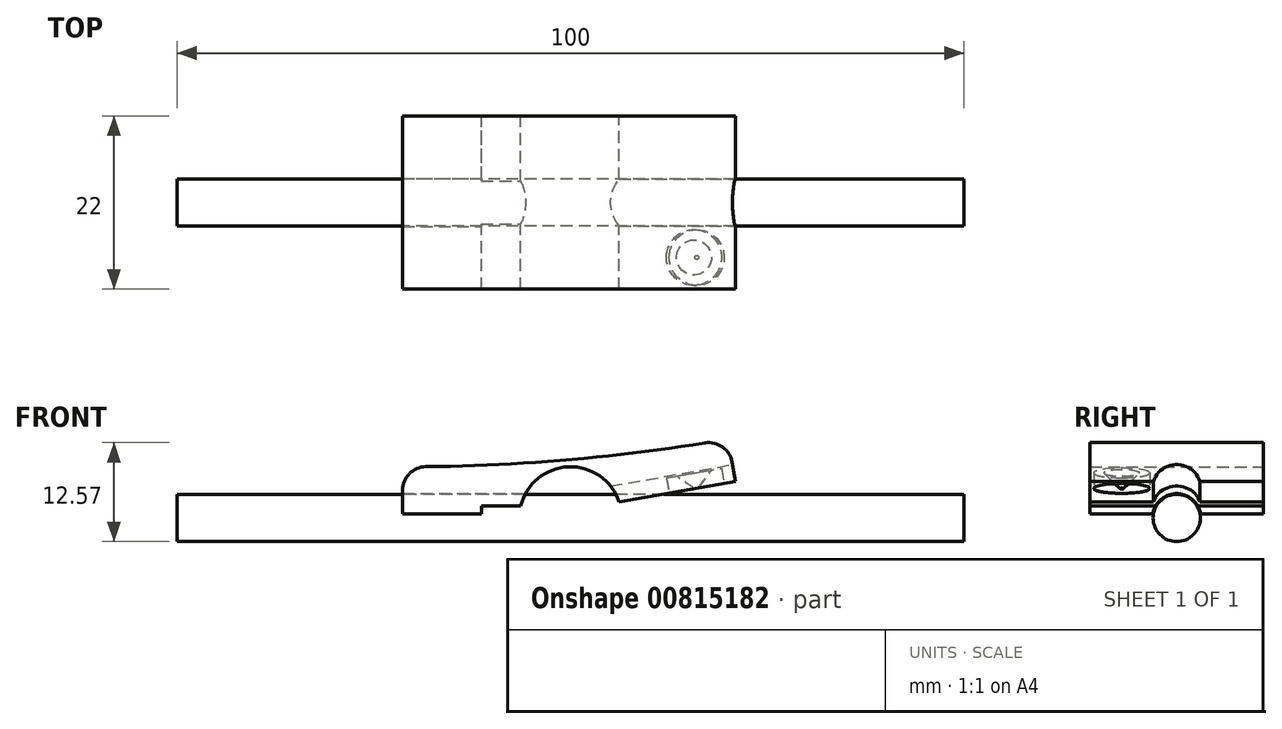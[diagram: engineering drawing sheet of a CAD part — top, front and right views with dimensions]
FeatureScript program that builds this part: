
annotation { "Feature Type Name" : "Feature", "Feature Type Description" : "" }
export const myFeature = defineFeature(function(context is Context, id is Id, definition is map)
    precondition{}
    {
        {
            var Q0;
            Q0=qCreatedBy(makeId("Front.planeOp"),FACE);
            var sketch = newSketch(context, id + "F0", { "sketchPlane" : qUnion([Q0])});
            skCircle(sketch, "E0", {"center": v(0, 0) * mm, "radius": 6.5 * mm});
            skLineSegment(sketch, "E1.bottom", {"start": v(-50, 3) * mm, "end": v(50, 3) * mm, "construction": true});
            skLineSegment(sketch, "E1.top", {"start": v(-50, -3) * mm, "end": v(50, -3) * mm, "construction": true});
            skLineSegment(sketch, "E1.left", {"start": v(-50, 3) * mm, "end": v(-50, -3) * mm, "construction": true});
            skLineSegment(sketch, "E1.right", {"start": v(50, 3) * mm, "end": v(50, -3) * mm, "construction": true});
            skLineSegment(sketch, "E2", {"start": v(-6.32, 1.5) * mm, "end": v(-11.32, 1.5) * mm});
            skLineSegment(sketch, "E3", {"start": v(-11.32, 1.5) * mm, "end": v(-11.32, 0.5) * mm});
            skLineSegment(sketch, "E4", {"start": v(-11.32, 0.5) * mm, "end": v(-21.32, 0.5) * mm});
            skLineSegment(sketch, "E5", {"start": v(-21.32, 0.5) * mm, "end": v(-21.32, 6.5) * mm});
            skLineSegment(sketch, "E6", {"start": v(-21.32, 6.5) * mm, "end": v(0, 6.5) * mm});
            skLineSegment(sketch, "E7.bottom", {"start": v(12, 5) * mm, "end": v(19, 5) * mm, "construction": true});
            skLineSegment(sketch, "E7.top", {"start": v(12, -5) * mm, "end": v(19, -5) * mm, "construction": true});
            skLineSegment(sketch, "E7.left", {"start": v(12, 5) * mm, "end": v(12, -5) * mm, "construction": true});
            skLineSegment(sketch, "E7.right", {"start": v(19, 5) * mm, "end": v(19, -5) * mm, "construction": true});
            skLineSegment(sketch, "E8", {"start": v(0, 6.5) * mm, "end": v(20, 10.03) * mm});
            skLineSegment(sketch, "E9", {"start": v(20, 10.03) * mm, "end": v(20.96, 4.61) * mm});
            skLineSegment(sketch, "E10", {"start": v(20.96, 4.61) * mm, "end": v(6.18, 2) * mm});
            skFitSpline(sketch, "E11", {"points": [v(20, 10.03) * mm, v(-21.32, 6.5) * mm], "startDerivative": vector(-40.82, -7.2) * mm, "endDerivative": vector(-41.45, 0) * mm});
            skSolve(sketch);
        }
        {
            var Q0;
            {var subQ0=sQuery(id+"F0.wireOp",EDGE,"E2");Q0=makeQuery(id+"F0.imprint","IMPRINT",FACE,{"disambiguationData":[TD([[makeQuery(id+"F0.imprint","IMPRINT",EDGE,{"derivedFrom":subQ0}),-1.0]])]});}
            var Q1;
            {var subQ0=sQuery(id+"F0.wireOp",EDGE,"E8");Q1=makeQuery(id+"F0.imprint","IMPRINT",FACE,{"disambiguationData":[TD([[makeQuery(id+"F0.imprint","IMPRINT",EDGE,{"derivedFrom":subQ0}),-1.0]])]});}
            var Q2;
            Q2=makeQuery(id+"F0.imprint","IMPRINT",FACE,{"disambiguationData":[TD([[makeQuery(id+"F0.imprint","IMPRINT",EDGE,{"derivedFrom":sQuery(id+"F0.wireOp",EDGE,"E6")}),1.0]])]});
            extrude(context, id + "F1", {"entities" : qUnion([Q0, Q1, Q2]), "endBound" : BoundingType.SYMMETRIC, "depth" : 22 * mm, "offsetDistance" : 25 * mm});
        }
        {
            var Q0;
            Q0=qCreatedBy(makeId("Right.planeOp"),FACE);
            var sketch = newSketch(context, id + "F2", { "sketchPlane" : qUnion([Q0])});
            skCircle(sketch, "E12", {"center": v(0, 0) * mm, "radius": 3.1 * mm});
            skSolve(sketch);
        }
        {
            var Q0;
            Q0 = qSketchRegion(id + "F2", true);
            extrude(context, id + "F3", {"entities" : qUnion([Q0]), "operationType" : NewBodyOperationType.REMOVE, "endBound" : BoundingType.SYMMETRIC, "oppositeDirection" : true, "depth" : 60 * mm, "offsetDistance" : 25 * mm});
        }
        {
            var Q0;
            Q0=makeQuery(id+"F1.opExtrude","SWEPT_FACE",FACE,{"disambiguationData":[OSD([sQuery(id+"F0.wireOp",EDGE,"E9")])]});
            var sketch = newSketch(context, id + "F4", { "sketchPlane" : qUnion([Q0])});
            skCircle(sketch, "E13", {"center": v(0, 0) * mm, "radius": 3.1 * mm});
            skSolve(sketch);
        }
        {
            var Q0;
            {var subQ0=sQuery(id+"F4.wireOp",EDGE,"E13");var subQ1=makeQuery(id+"F1.opExtrude","SWEPT_EDGE",EDGE,{"disambiguationData":[OSD([sQuery(id+"F0.wireOp",EDGE,"E9"),sQuery(id+"F0.wireOp",EDGE,"E10")])]});var subQ2=makeQuery(id+"F4.imprint","INTERSECT",VERTEX,{"disambiguationData":[OD(0.0)],"derivedFrom":[subQ1,subQ0]});Q0=makeQuery(id+"F4.imprint","IMPRINT",FACE,{"disambiguationData":[TD([[makeQuery(id+"F4.imprint","IMPRINT",EDGE,{"disambiguationData":[TD([[subQ2,1.0]])],"derivedFrom":subQ0}),1.0]])]});}
            var Q1;
            {var subQ0=sQuery(id+"F4.wireOp",EDGE,"E13");var subQ1=makeQuery(id+"F1.opExtrude","SWEPT_EDGE",EDGE,{"disambiguationData":[OSD([sQuery(id+"F0.wireOp",EDGE,"E9"),sQuery(id+"F0.wireOp",EDGE,"E10")])]});var subQ2=makeQuery(id+"F4.imprint","INTERSECT",VERTEX,{"disambiguationData":[OD(0.0)],"derivedFrom":[subQ1,subQ0]});Q1=makeQuery(id+"F4.imprint","IMPRINT",FACE,{"disambiguationData":[TD([[makeQuery(id+"F4.imprint","IMPRINT",EDGE,{"disambiguationData":[TD([[subQ2,-1.0]])],"derivedFrom":subQ0}),1.0]])]});}
            extrude(context, id + "F5", {"entities" : qUnion([Q0, Q1]), "operationType" : NewBodyOperationType.REMOVE, "oppositeDirection" : true, "depth" : 60 * mm, "offsetDistance" : 25 * mm});
        }
        {
            var Q0;
            Q0=qCreatedBy(makeId("Right.planeOp"),FACE);
            var sketch = newSketch(context, id + "F6", { "sketchPlane" : qUnion([Q0])});
            skCircle(sketch, "E14", {"center": v(0, 0) * mm, "radius": 3 * mm});
            skSolve(sketch);
        }
        {
            var Q0;
            Q0 = qSketchRegion(id + "F6", true);
            extrude(context, id + "F7", {"entities" : qUnion([Q0]), "endBound" : BoundingType.SYMMETRIC, "depth" : 100 * mm, "offsetDistance" : 25 * mm});
        }
        {
            var Q0;
            {var subQ0=sQuery(id+"F0.wireOp",EDGE,"E0");var subQ1=sQuery(id+"F0.wireOp",EDGE,"E10");var subQ2=sQuery(id+"F0.wireOp",EDGE,"E9");Q0=makeQuery(id+"F5.boolean.opBoolean","SPLIT",FACE,{"disambiguationData":[TD([makeQuery(id+"F1.opExtrude","CAP_FACE",FACE,{"disambiguationData":[OSD([subQ0,sQuery(id+"F0.wireOp",EDGE,"E2"),sQuery(id+"F0.wireOp",EDGE,"E3"),sQuery(id+"F0.wireOp",EDGE,"E4"),sQuery(id+"F0.wireOp",EDGE,"E5"),sQuery(id+"F0.wireOp",EDGE,"E6"),sQuery(id+"F0.wireOp",EDGE,"E8"),subQ2,subQ1])],"isStart":false})])],"derivedFrom":makeQuery(id+"F1.opExtrude","SWEPT_FACE",FACE,{"disambiguationData":[OSD([subQ1])]})});}
            var sketch = newSketch(context, id + "F8", { "sketchPlane" : qUnion([Q0])});
            skCircle(sketch, "E15", {"center": v(16.44, 6.98) * mm, "radius": 3.55 * mm});
            skPoint(sketch, "E15.centerSnap0", {"position": v(21.44, 6.98) * mm});
            skCircle(sketch, "E16", {"center": v(16.44, 6.98) * mm, "radius": 2.25 * mm});
            skCircle(sketch, "E17.MirrorC", {"center": v(16.44, -6.98) * mm, "radius": 3.55 * mm});
            skCircle(sketch, "E18.MirrorC", {"center": v(16.44, -6.98) * mm, "radius": 2.25 * mm});
            skSolve(sketch);
        }
        {
            var Q0;
            Q0=makeQuery(id+"F8.imprint","IMPRINT",FACE,{"disambiguationData":[TD([[makeQuery(id+"F8.imprint","IMPRINT",EDGE,{"derivedFrom":sQuery(id+"F8.wireOp",EDGE,"E15")}),1.0]])]});
            var Q1;
            Q1=makeQuery(id+"F8.imprint","IMPRINT",FACE,{"disambiguationData":[TD([[makeQuery(id+"F8.imprint","IMPRINT",EDGE,{"derivedFrom":sQuery(id+"F8.wireOp",EDGE,"E17.MirrorC")}),-1.0]])]});
            extrude(context, id + "F9", {"entities" : qUnion([Q0, Q1]), "operationType" : NewBodyOperationType.REMOVE, "oppositeDirection" : true, "depth" : 2 * mm, "offsetDistance" : 25 * mm});
        }
        {
            var Q0;
            Q0=makeQuery(id+"F9.boolean.opBoolean","COPY",EDGE,{"derivedFrom":makeQuery(id+"F9.opExtrude","CAP_EDGE",EDGE,{"disambiguationData":[OSD([sQuery(id+"F8.wireOp",EDGE,"E16")])],"isStart":true})});
            var Q1;
            Q1=makeQuery(id+"F9.boolean.opBoolean","COPY",EDGE,{"derivedFrom":makeQuery(id+"F9.opExtrude","CAP_EDGE",EDGE,{"disambiguationData":[OSD([sQuery(id+"F8.wireOp",EDGE,"E18.MirrorC")])],"isStart":true})});
            chamfer(context, id + "F10", {"entities" : qUnion([Q0, Q1]), "width" : 2 * mm, "tangentPropagation" : true});
        }
        {
            var Q0;
            Q0=makeQuery(id+"F1.opExtrude","SWEPT_EDGE",EDGE,{"disambiguationData":[OSD([sQuery(id+"F0.wireOp",EDGE,"E8"),sQuery(id+"F0.wireOp",EDGE,"E9")])]});
            var Q1;
            Q1=makeQuery(id+"F1.opExtrude","SWEPT_EDGE",EDGE,{"disambiguationData":[OSD([sQuery(id+"F0.wireOp",EDGE,"E5"),sQuery(id+"F0.wireOp",EDGE,"E6")])]});
            fillet(context, id + "F11", {"entities" : qUnion([Q0, Q1]), "radius" : 3 * mm, "tangentPropagation" : true, "allowEdgeOverflow" : false});
        }
    });
